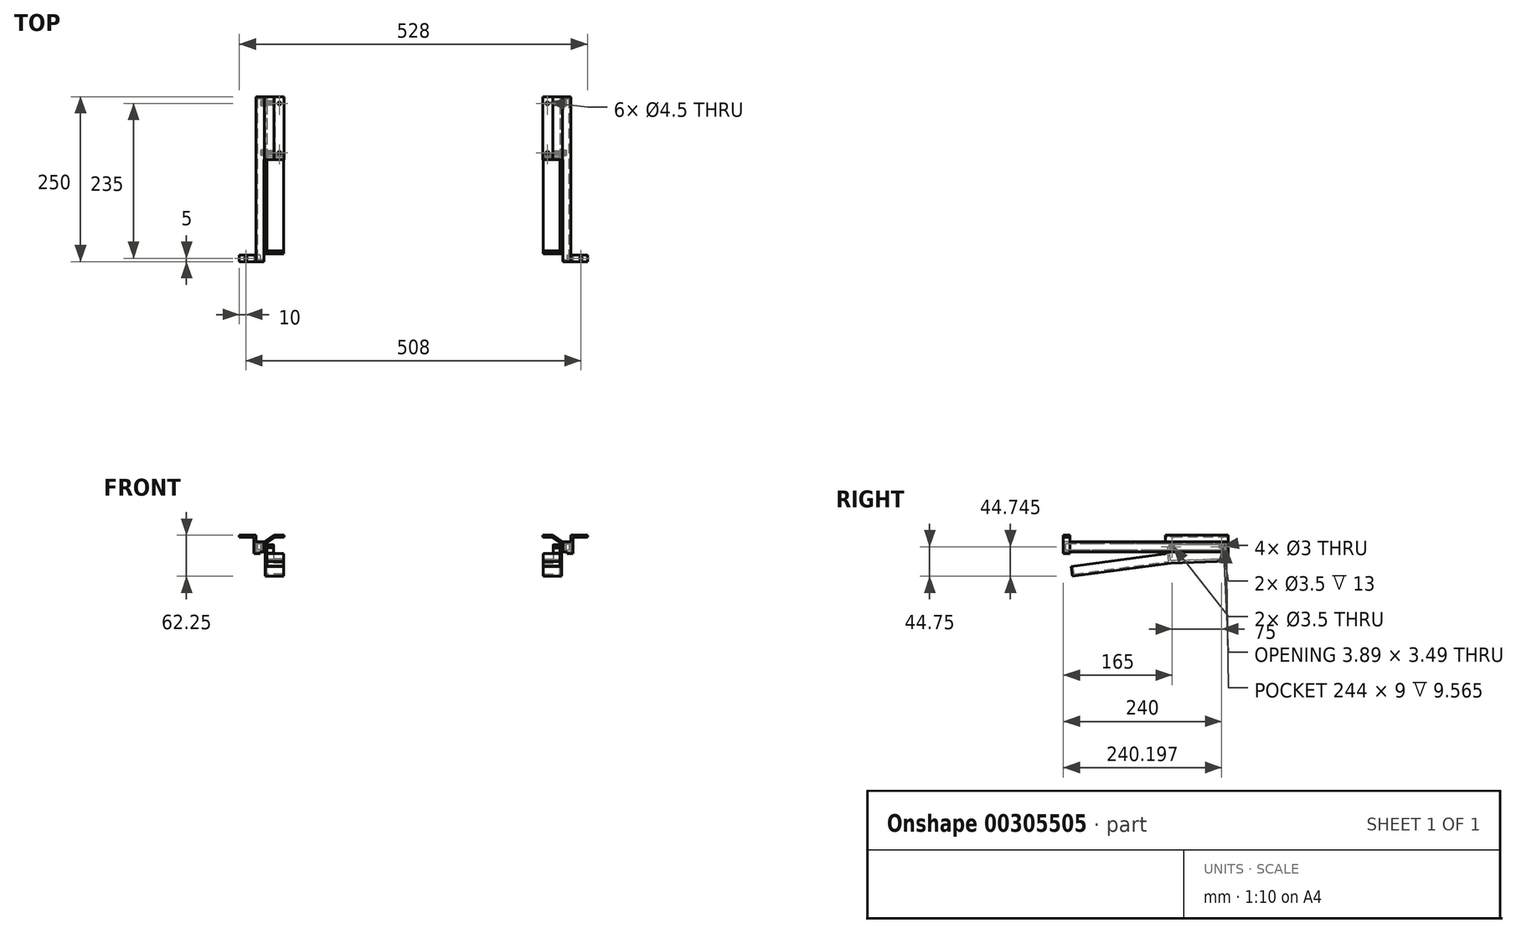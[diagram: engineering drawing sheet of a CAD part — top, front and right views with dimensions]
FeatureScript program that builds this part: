
annotation { "Feature Type Name" : "Feature", "Feature Type Description" : "" }
export const myFeature = defineFeature(function(context is Context, id is Id, definition is map)
    precondition{}
    {
        {
            var Q0;
            Q0=qCreatedBy(makeId("Right.planeOp"),FACE);
            var sketch = newSketch(context, id + "F0", { "sketchPlane" : qUnion([Q0])});
            skCircle(sketch, "E0", {"center": v(0, 0) * mm, "radius": 1.5 * mm});
            skCircle(sketch, "E1", {"center": v(0, 0) * mm, "radius": 4 * mm});
            skCircle(sketch, "E2.1.0.0", {"center": v(75, 0) * mm, "radius": 4 * mm});
            skCircle(sketch, "E2.1.0.1", {"center": v(75, 0) * mm, "radius": 1.5 * mm});
            skLineSegment(sketch, "E2.direction1", {"start": v(0, 0) * mm, "end": v(75, 0) * mm, "construction": true});
            skSolve(sketch);
        }
        {
            var Q0;
            Q0=makeQuery(id+"F0.imprint","IMPRINT",FACE,{"disambiguationData":[TD([[makeQuery(id+"F0.imprint","IMPRINT",EDGE,{"derivedFrom":sQuery(id+"F0.wireOp",EDGE,"E0")}),-1.0]])]});
            var Q1;
            Q1=makeQuery(id+"F0.imprint","IMPRINT",FACE,{"disambiguationData":[TD([[makeQuery(id+"F0.imprint","IMPRINT",EDGE,{"derivedFrom":sQuery(id+"F0.wireOp",EDGE,"E2.1.0.0")}),1.0]])]});
            extrude(context, id + "F1", {"entities" : qUnion([Q0, Q1]), "endBound" : BoundingType.SYMMETRIC, "depth" : 3 * mm});
        }
        {
            var Q0;
            Q0=qCreatedBy(makeId("Right.planeOp"),FACE);
            cPlane(context, id + "F2", {"entities" : qUnion([Q0]), "cplaneType" : CPlaneType.OFFSET, "offset" : 9 * mm, "oppositeDirection" : true, "width" : 150 * mm, "height" : 150 * mm});
        }
        {
            var Q0;
            Q0=qCreatedBy(id+"F2.planeOp",FACE);
            var sketch = newSketch(context, id + "F3", { "sketchPlane" : qUnion([Q0])});
            skLineSegment(sketch, "E3", {"start": v(0, 0) * mm, "end": v(0, 7.5) * mm, "construction": true});
            skLineSegment(sketch, "E4", {"start": v(0, 0) * mm, "end": v(85, 0) * mm, "construction": true});
            skLineSegment(sketch, "E5", {"start": v(85, 0) * mm, "end": v(85, 7.5) * mm});
            skLineSegment(sketch, "E6", {"start": v(85, 7.5) * mm, "end": v(-165, 7.5) * mm});
            skLineSegment(sketch, "E7", {"start": v(-165, 7.5) * mm, "end": v(-165, -7.5) * mm});
            skLineSegment(sketch, "E8", {"start": v(-165, -7.5) * mm, "end": v(85, -7.5) * mm});
            skLineSegment(sketch, "E9", {"start": v(85, -7.5) * mm, "end": v(85, 0) * mm});
            skSolve(sketch);
        }
        {
            var Q0;
            Q0=makeQuery(id+"F3.imprint","IMPRINT",FACE,{"disambiguationData":[TD([[makeQuery(id+"F3.imprint","IMPRINT",EDGE,{"derivedFrom":sQuery(id+"F3.wireOp",EDGE,"E5")}),1.0]])]});
            extrude(context, id + "F4", {"entities" : qUnion([Q0]), "depth" : 3 * mm});
        }
        {
            var Q0;
            Q0=makeQuery(id+"F4.opExtrude","CAP_FACE",FACE,{"disambiguationData":[OSD([sQuery(id+"F3.wireOp",EDGE,"E5"),sQuery(id+"F3.wireOp",EDGE,"E6"),sQuery(id+"F3.wireOp",EDGE,"E7"),sQuery(id+"F3.wireOp",EDGE,"E8"),sQuery(id+"F3.wireOp",EDGE,"E9")])],"isStart":false});
            var sketch = newSketch(context, id + "F5", { "sketchPlane" : qUnion([Q0])});
            skLineSegment(sketch, "E10", {"start": v(-165, 7.5) * mm, "end": v(85, 7.5) * mm});
            skLineSegment(sketch, "E11", {"start": v(85, 7.5) * mm, "end": v(85, 4.5) * mm});
            skLineSegment(sketch, "E12", {"start": v(85, 4.5) * mm, "end": v(-165, 4.5) * mm});
            skLineSegment(sketch, "E13", {"start": v(-165, 4.5) * mm, "end": v(-165, 7.5) * mm});
            skSolve(sketch);
        }
        {
            var Q0;
            Q0=makeQuery(id+"F5.imprint","IMPRINT",FACE,{"disambiguationData":[TD([[makeQuery(id+"F5.imprint","IMPRINT",EDGE,{"derivedFrom":sQuery(id+"F5.wireOp",EDGE,"E10")}),1.0]])]});
            extrude(context, id + "F6", {"entities" : qUnion([Q0]), "operationType" : NewBodyOperationType.ADD, "depth" : 10 * mm});
        }
        {
            var Q0;
            Q0=makeQuery(id+"F4.opExtrude","CAP_FACE",FACE,{"disambiguationData":[OSD([sQuery(id+"F3.wireOp",EDGE,"E5"),sQuery(id+"F3.wireOp",EDGE,"E6"),sQuery(id+"F3.wireOp",EDGE,"E7"),sQuery(id+"F3.wireOp",EDGE,"E8"),sQuery(id+"F3.wireOp",EDGE,"E9")])],"isStart":false});
            var sketch = newSketch(context, id + "F7", { "sketchPlane" : qUnion([Q0])});
            skLineSegment(sketch, "E14", {"start": v(-165, 4.5) * mm, "end": v(-165, -7.5) * mm});
            skLineSegment(sketch, "E15", {"start": v(-165, -7.5) * mm, "end": v(85, -7.5) * mm});
            skLineSegment(sketch, "E16", {"start": v(85, -7.5) * mm, "end": v(85, 4.5) * mm});
            skLineSegment(sketch, "E17.0", {"start": v(82, -4.5) * mm, "end": v(82, 4.5) * mm});
            skLineSegment(sketch, "E17.1", {"start": v(-162, -4.5) * mm, "end": v(82, -4.5) * mm});
            skLineSegment(sketch, "E17.2", {"start": v(-162, 4.5) * mm, "end": v(-162, -4.5) * mm});
            skLineSegment(sketch, "E18", {"start": v(-165, 4.5) * mm, "end": v(-162, 4.5) * mm});
            skLineSegment(sketch, "E19", {"start": v(82, 4.5) * mm, "end": v(85, 4.5) * mm});
            skSolve(sketch);
        }
        {
            var Q0;
            Q0=makeQuery(id+"F7.imprint","IMPRINT",FACE,{"disambiguationData":[TD([[makeQuery(id+"F7.imprint","IMPRINT",EDGE,{"derivedFrom":sQuery(id+"F7.wireOp",EDGE,"E14")}),1.0]])]});
            extrude(context, id + "F8", {"entities" : qUnion([Q0]), "operationType" : NewBodyOperationType.ADD, "depth" : 10 * mm});
        }
        {
            var Q0;
            Q0=qCreatedBy(makeId("Right.planeOp"),FACE);
            cPlane(context, id + "F9", {"entities" : qUnion([Q0]), "cplaneType" : CPlaneType.OFFSET, "offset" : 5 * mm, "width" : 150 * mm, "height" : 150 * mm});
        }
        {
            var Q0;
            Q0=qCreatedBy(id+"F9.planeOp",FACE);
            var sketch = newSketch(context, id + "F10", { "sketchPlane" : qUnion([Q0])});
            skLineSegment(sketch, "E20", {"start": v(0, 0) * mm, "end": v(85, 0) * mm, "construction": true});
            skLineSegment(sketch, "E21", {"start": v(85, 0) * mm, "end": v(85, 3) * mm, "construction": true});
            skLineSegment(sketch, "E22", {"start": v(85, 3) * mm, "end": v(-5, 3) * mm});
            skLineSegment(sketch, "E23", {"start": v(-5, 3) * mm, "end": v(-155, 3) * mm, "construction": true});
            skLineSegment(sketch, "E24", {"start": v(-155, 3) * mm, "end": v(-155, -17) * mm, "construction": true});
            skLineSegment(sketch, "E25", {"start": v(-155, -17) * mm, "end": v(-5, 3) * mm});
            skLineSegment(sketch, "E26", {"start": v(-155, -17) * mm, "end": v(-151.3, -44.75) * mm});
            skLineSegment(sketch, "E27", {"start": v(-151.3, -44.75) * mm, "end": v(85, -34.74) * mm});
            skLineSegment(sketch, "E28", {"start": v(85, 3) * mm, "end": v(85, -34.74) * mm});
            skSolve(sketch);
        }
        {
            var Q0;
            Q0=makeQuery(id+"F10.imprint","IMPRINT",FACE,{"disambiguationData":[TD([[makeQuery(id+"F10.imprint","IMPRINT",EDGE,{"derivedFrom":sQuery(id+"F10.wireOp",EDGE,"E22")}),1.0]])]});
            extrude(context, id + "F11", {"entities" : qUnion([Q0]), "depth" : 3 * mm});
        }
        {
            var Q0;
            Q0=makeQuery(id+"F11.opExtrude","CAP_FACE",FACE,{"disambiguationData":[OSD([sQuery(id+"F10.wireOp",EDGE,"E22"),sQuery(id+"F10.wireOp",EDGE,"E25"),sQuery(id+"F10.wireOp",EDGE,"E26"),sQuery(id+"F10.wireOp",EDGE,"E27"),sQuery(id+"F10.wireOp",EDGE,"E28")])],"isStart":false});
            var sketch = newSketch(context, id + "F12", { "sketchPlane" : qUnion([Q0])});
            skLineSegment(sketch, "E29", {"start": v(0, 0) * mm, "end": v(75, 0) * mm, "construction": true});
            skCircle(sketch, "E30", {"center": v(0, 0) * mm, "radius": 1.75 * mm});
            skCircle(sketch, "E31", {"center": v(75, 0) * mm, "radius": 1.75 * mm});
            skSolve(sketch);
        }
        {
            var Q0;
            Q0=makeQuery(id+"F12.imprint","IMPRINT",FACE,{"disambiguationData":[TD([[makeQuery(id+"F12.imprint","IMPRINT",EDGE,{"derivedFrom":sQuery(id+"F12.wireOp",EDGE,"E30")}),1.0]])]});
            var Q1;
            Q1=makeQuery(id+"F12.imprint","IMPRINT",FACE,{"disambiguationData":[TD([[makeQuery(id+"F12.imprint","IMPRINT",EDGE,{"derivedFrom":sQuery(id+"F12.wireOp",EDGE,"E31")}),1.0]])]});
            extrude(context, id + "F13", {"entities" : qUnion([Q0, Q1]), "operationType" : NewBodyOperationType.REMOVE, "endBound" : BoundingType.UP_TO_NEXT, "oppositeDirection" : true, "depth" : 25 * mm});
        }
        {
            var Q0;
            Q0=makeQuery(id+"F11.opExtrude","CAP_FACE",FACE,{"disambiguationData":[OSD([sQuery(id+"F10.wireOp",EDGE,"E22"),sQuery(id+"F10.wireOp",EDGE,"E25"),sQuery(id+"F10.wireOp",EDGE,"E26"),sQuery(id+"F10.wireOp",EDGE,"E27"),sQuery(id+"F10.wireOp",EDGE,"E28")])],"isStart":false});
            var sketch = newSketch(context, id + "F14", { "sketchPlane" : qUnion([Q0])});
            skLineSegment(sketch, "E32", {"start": v(-151.3, -44.75) * mm, "end": v(-153.28, -29.89) * mm});
            skLineSegment(sketch, "E33", {"start": v(-153.28, -29.89) * mm, "end": v(-150.3, -29.49) * mm});
            skLineSegment(sketch, "E34.0", {"start": v(-148.72, -41.38) * mm, "end": v(-150.3, -29.49) * mm});
            skLineSegment(sketch, "E35", {"start": v(-148.72, -41.38) * mm, "end": v(-5, -22.22) * mm});
            skLineSegment(sketch, "E36", {"start": v(-5, -22.22) * mm, "end": v(-6.58, -10.33) * mm});
            skLineSegment(sketch, "E37.0", {"start": v(-2.09, -21.33) * mm, "end": v(-3.57, -10.19) * mm});
            skLineSegment(sketch, "E37.1", {"start": v(-151.3, -44.75) * mm, "end": v(-1.62, -24.8) * mm});
            skLineSegment(sketch, "E38", {"start": v(-6.58, -10.33) * mm, "end": v(-3.57, -10.19) * mm});
            skLineSegment(sketch, "E39", {"start": v(-1.62, -24.8) * mm, "end": v(85, -21.77) * mm});
            skLineSegment(sketch, "E40", {"start": v(85, -21.77) * mm, "end": v(85, -18.77) * mm});
            skLineSegment(sketch, "E41", {"start": v(85, -18.77) * mm, "end": v(-2.09, -21.33) * mm});
            skPoint(sketch, "E42.trimOffspring.end.orphan", {"position": v(-32.21, -22.22) * mm});
            skSolve(sketch);
        }
        {
            var Q0;
            Q0=makeQuery(id+"F14.imprint","IMPRINT",FACE,{"disambiguationData":[TD([[makeQuery(id+"F14.imprint","IMPRINT",EDGE,{"derivedFrom":sQuery(id+"F14.wireOp",EDGE,"E32")}),1.0]])]});
            extrude(context, id + "F15", {"entities" : qUnion([Q0]), "operationType" : NewBodyOperationType.ADD, "depth" : 25 * mm});
        }
        {
            var Q0;
            Q0=qCreatedBy(id+"F9.planeOp",FACE);
            cPlane(context, id + "F16", {"entities" : qUnion([Q0]), "cplaneType" : CPlaneType.OFFSET, "offset" : 225 * mm, "width" : 150 * mm, "height" : 150 * mm});
        }
        {
            var Q0;
            Q0=makeQuery(id+"F4.opExtrude","SWEPT_BODY",BODY,{"disambiguationData":[OSD([sQuery(id+"F3.wireOp",EDGE,"E5"),sQuery(id+"F3.wireOp",EDGE,"E6"),sQuery(id+"F3.wireOp",EDGE,"E7"),sQuery(id+"F3.wireOp",EDGE,"E8"),sQuery(id+"F3.wireOp",EDGE,"E9")])]});
            var Q1;
            Q1=makeQuery(id+"F11.opExtrude","SWEPT_BODY",BODY,{"disambiguationData":[OSD([sQuery(id+"F10.wireOp",EDGE,"E22"),sQuery(id+"F10.wireOp",EDGE,"E25"),sQuery(id+"F10.wireOp",EDGE,"E26"),sQuery(id+"F10.wireOp",EDGE,"E27"),sQuery(id+"F10.wireOp",EDGE,"E28")])]});
            var Q2;
            Q2=makeQuery(id+"F1.opExtrude","SWEPT_BODY",BODY,{"disambiguationData":[OSD([sQuery(id+"F0.wireOp",EDGE,"E0"),sQuery(id+"F0.wireOp",EDGE,"E1")])]});
            var Q3;
            Q3=makeQuery(id+"F1.opExtrude","SWEPT_BODY",BODY,{"disambiguationData":[OSD([sQuery(id+"F0.wireOp",EDGE,"E2.1.0.0"),sQuery(id+"F0.wireOp",EDGE,"E2.1.0.1")])]});
            var Q4;
            Q4=qCreatedBy(id+"F16.planeOp",FACE);
            mirror(context, id + "F17", {"entities" : qUnion([Q0, Q1, Q2, Q3]), "mirrorPlane" : qUnion([Q4])});
        }
        {
            var Q0;
            Q0=makeQuery(id+"F11.opExtrude","CAP_FACE",FACE,{"disambiguationData":[OSD([sQuery(id+"F10.wireOp",EDGE,"E22"),sQuery(id+"F10.wireOp",EDGE,"E25"),sQuery(id+"F10.wireOp",EDGE,"E26"),sQuery(id+"F10.wireOp",EDGE,"E27"),sQuery(id+"F10.wireOp",EDGE,"E28")])],"isStart":false});
            var sketch = newSketch(context, id + "F18", { "sketchPlane" : qUnion([Q0])});
            skArc(sketch, "E43", {"start": v(0.94, -1.47) * mm, "mid": v(0.78, 1.57) * mm, "end": v(-1.74, -0.14) * mm});
            skArc(sketch, "E44", {"start": v(0, -3) * mm, "mid": v(0.64, 2.93) * mm, "end": v(-1.25, -2.73) * mm});
            skLineSegment(sketch, "E45", {"start": v(0, 0) * mm, "end": v(0, -31.78) * mm, "construction": true});
            skLineSegment(sketch, "E46.1.0.0", {"start": v(76.5, -2.79) * mm, "end": v(76.7, -19.01) * mm});
            skLineSegment(sketch, "E46.1.0.1", {"start": v(74.14, -2.73) * mm, "end": v(73.42, -19.1) * mm});
            skLineSegment(sketch, "E46.1.0.2", {"start": v(75.4, 0) * mm, "end": v(75.4, -31.78) * mm, "construction": true});
            skCircle(sketch, "E46.1.0.4", {"center": v(75.4, 0) * mm, "radius": 1.75 * mm});
            skLineSegment(sketch, "E46.1.0.5", {"start": v(73.42, -19.1) * mm, "end": v(76.7, -19.01) * mm});
            skLineSegment(sketch, "E46.direction1", {"start": v(-1.58, -19.1) * mm, "end": v(73.42, -19.1) * mm, "construction": true});
            skLineSegment(sketch, "E47", {"start": v(-5.08, -10.26) * mm, "end": v(0, 0) * mm, "construction": true});
            skLineSegment(sketch, "E48.0", {"start": v(-6.6, -9.95) * mm, "end": v(-1.74, -0.14) * mm});
            skLineSegment(sketch, "E49.0", {"start": v(-3.02, -9.48) * mm, "end": v(0.94, -1.47) * mm});
            skLineSegment(sketch, "E50", {"start": v(-6.58, -10.33) * mm, "end": v(-6.6, -9.95) * mm});
            skLineSegment(sketch, "E51", {"start": v(-6.58, -10.33) * mm, "end": v(-3.57, -10.19) * mm});
            skLineSegment(sketch, "E52", {"start": v(-3.57, -10.19) * mm, "end": v(-3.02, -9.48) * mm});
            skPoint(sketch, "E53.orphan", {"position": v(-6.78, -10.33) * mm});
            skPoint(sketch, "E54.orphan", {"position": v(-3.37, -10.19) * mm});
            skPoint(sketch, "E55.orphan", {"position": v(76.5, -2.6) * mm});
            skPoint(sketch, "E56.orphan", {"position": v(75.4, -3) * mm});
            skArc(sketch, "E57", {"start": v(76.5, -2.79) * mm, "mid": v(75.47, 3) * mm, "end": v(74.14, -2.73) * mm});
            skSolve(sketch);
        }
        {
            var Q0;
            {var subQ10=sQuery(id+"F18.wireOp",EDGE,"E50");Q0=makeQuery(id+"F18.imprint","IMPRINT",FACE,{"disambiguationData":[TD([[makeQuery(id+"F18.imprint","IMPRINT",EDGE,{"derivedFrom":subQ10}),-1.0]])]});}
            var Q1;
            {var subQ1=sQuery(id+"F18.wireOp",EDGE,"E43");Q1=makeQuery(id+"F18.imprint","IMPRINT",FACE,{"disambiguationData":[TD([[makeQuery(id+"F18.imprint","IMPRINT",EDGE,{"derivedFrom":subQ1}),-1.0]])]});}
            var Q2;
            {var subQ6=sQuery(id+"F18.wireOp",EDGE,"E46.1.0.0");Q2=makeQuery(id+"F18.imprint","IMPRINT",FACE,{"disambiguationData":[TD([[makeQuery(id+"F18.imprint","IMPRINT",EDGE,{"derivedFrom":subQ6}),-1.0]])]});}
            extrude(context, id + "F19", {"entities" : qUnion([Q0, Q1, Q2]), "operationType" : NewBodyOperationType.ADD, "depth" : 10 * mm});
        }
        {
            var Q0;
            Q0=makeQuery(id+"F17.opPattern","COPY",BODY,{"derivedFrom":makeQuery(id+"F11.opExtrude","SWEPT_BODY",BODY,{"disambiguationData":[OSD([sQuery(id+"F10.wireOp",EDGE,"E22"),sQuery(id+"F10.wireOp",EDGE,"E25"),sQuery(id+"F10.wireOp",EDGE,"E26"),sQuery(id+"F10.wireOp",EDGE,"E27"),sQuery(id+"F10.wireOp",EDGE,"E28")])]}),"instanceName":"1"});
            deleteBodies(context, id + "F20", {"entities" : qUnion([Q0])});
        }
        {
            var Q0;
            Q0=makeQuery(id+"F11.opExtrude","SWEPT_BODY",BODY,{"disambiguationData":[OSD([sQuery(id+"F10.wireOp",EDGE,"E22"),sQuery(id+"F10.wireOp",EDGE,"E25"),sQuery(id+"F10.wireOp",EDGE,"E26"),sQuery(id+"F10.wireOp",EDGE,"E27"),sQuery(id+"F10.wireOp",EDGE,"E28")])]});
            var Q1;
            Q1=qCreatedBy(id+"F16.planeOp",FACE);
            mirror(context, id + "F21", {"entities" : qUnion([Q0]), "mirrorPlane" : qUnion([Q1])});
        }
        {
            var Q0;
            Q0=makeQuery(id+"F21.opPattern","COPY",BODY,{"derivedFrom":makeQuery(id+"F11.opExtrude","SWEPT_BODY",BODY,{"disambiguationData":[OSD([sQuery(id+"F10.wireOp",EDGE,"E22"),sQuery(id+"F10.wireOp",EDGE,"E25"),sQuery(id+"F10.wireOp",EDGE,"E26"),sQuery(id+"F10.wireOp",EDGE,"E27"),sQuery(id+"F10.wireOp",EDGE,"E28")])]}),"instanceName":"1"});
            deleteBodies(context, id + "F22", {"entities" : qUnion([Q0])});
        }
        {
            var Q0;
            {var subQ0=sQuery(id+"F10.wireOp",EDGE,"E28");var subQ1=sQuery(id+"F10.wireOp",EDGE,"E27");var subQ2=sQuery(id+"F10.wireOp",EDGE,"E26");Q0=makeQuery(id+"F15.boolean.opBoolean","SPLIT",FACE,{"disambiguationData":[TD([makeQuery(id+"F11.opExtrude","SWEPT_FACE",FACE,{"disambiguationData":[OSD([subQ1])]})])],"derivedFrom":makeQuery(id+"F11.opExtrude","CAP_FACE",FACE,{"disambiguationData":[OSD([sQuery(id+"F10.wireOp",EDGE,"E22"),sQuery(id+"F10.wireOp",EDGE,"E25"),subQ2,subQ1,subQ0])],"isStart":false})});}
            var sketch = newSketch(context, id + "F23", { "sketchPlane" : qUnion([Q0])});
            skLineSegment(sketch, "E58", {"start": v(-151.3, -44.75) * mm, "end": v(-1.62, -24.8) * mm});
            skLineSegment(sketch, "E59", {"start": v(-1.62, -24.8) * mm, "end": v(85, -21.77) * mm});
            skLineSegment(sketch, "E60", {"start": v(85, -21.77) * mm, "end": v(85, -34.74) * mm});
            skLineSegment(sketch, "E61", {"start": v(85, -34.74) * mm, "end": v(-151.3, -44.75) * mm});
            skSolve(sketch);
        }
        {
            var Q0;
            Q0=makeQuery(id+"F23.imprint","IMPRINT",FACE,{"disambiguationData":[TD([[makeQuery(id+"F23.imprint","IMPRINT",EDGE,{"derivedFrom":sQuery(id+"F23.wireOp",EDGE,"E58")}),-1.0]])]});
            extrude(context, id + "F24", {"entities" : qUnion([Q0]), "operationType" : NewBodyOperationType.REMOVE, "endBound" : BoundingType.UP_TO_NEXT, "oppositeDirection" : true, "depth" : 25 * mm});
        }
        {
            var Q0;
            Q0=makeQuery(id+"F11.opExtrude","SWEPT_BODY",BODY,{"disambiguationData":[OSD([sQuery(id+"F10.wireOp",EDGE,"E22"),sQuery(id+"F10.wireOp",EDGE,"E25"),sQuery(id+"F10.wireOp",EDGE,"E26"),sQuery(id+"F10.wireOp",EDGE,"E27"),sQuery(id+"F10.wireOp",EDGE,"E28")])]});
            var Q1;
            Q1=qCreatedBy(id+"F16.planeOp",FACE);
            mirror(context, id + "F25", {"entities" : qUnion([Q0]), "mirrorPlane" : qUnion([Q1])});
        }
        {
            var Q0;
            Q0=makeQuery(id+"F8.boolean.opBoolean","MERGE",FACE,{"derivedFrom":[makeQuery(id+"F6.boolean.opBoolean","MERGE",FACE,{"derivedFrom":[makeQuery(id+"F4.opExtrude","SWEPT_FACE",FACE,{"disambiguationData":[OSD([sQuery(id+"F3.wireOp",EDGE,"E7")])]}),makeQuery(id+"F6.opExtrude","SWEPT_FACE",FACE,{"disambiguationData":[OSD([sQuery(id+"F5.wireOp",EDGE,"E13")])]})]}),makeQuery(id+"F8.opExtrude","SWEPT_FACE",FACE,{"disambiguationData":[OSD([sQuery(id+"F7.wireOp",EDGE,"E14")])]})]});
            var sketch = newSketch(context, id + "F26", { "sketchPlane" : qUnion([Q0])});
            skLineSegment(sketch, "E62", {"start": v(4, 7.5) * mm, "end": v(18.76, 17.5) * mm});
            skLineSegment(sketch, "E63", {"start": v(18.76, 17.5) * mm, "end": v(33.76, 17.5) * mm});
            skLineSegment(sketch, "E64", {"start": v(33.76, 17.5) * mm, "end": v(33.76, 14.5) * mm});
            skLineSegment(sketch, "E65.0", {"start": v(19.68, 14.5) * mm, "end": v(33.76, 14.5) * mm});
            skLineSegment(sketch, "E65.1", {"start": v(5.68, 5.02) * mm, "end": v(19.68, 14.5) * mm});
            skLineSegment(sketch, "E66", {"start": v(5.68, 5.02) * mm, "end": v(4.93, 4.5) * mm});
            skLineSegment(sketch, "E67", {"start": v(4, 4.5) * mm, "end": v(4, 7.5) * mm});
            skLineSegment(sketch, "E68", {"start": v(4.93, 4.5) * mm, "end": v(4, 4.5) * mm});
            skSolve(sketch);
        }
        {
            var Q0;
            Q0=makeQuery(id+"F26.imprint","IMPRINT",FACE,{"disambiguationData":[TD([[makeQuery(id+"F26.imprint","IMPRINT",EDGE,{"derivedFrom":sQuery(id+"F26.wireOp",EDGE,"E62")}),-1.0]])]});
            extrude(context, id + "F27", {"entities" : qUnion([Q0]), "operationType" : NewBodyOperationType.ADD, "oppositeDirection" : true, "depth" : 250 * mm});
        }
        {
            var Q0;
            Q0=makeQuery(id+"F27.opExtrude","SWEPT_FACE",FACE,{"disambiguationData":[OSD([sQuery(id+"F26.wireOp",EDGE,"E63")])]});
            var sketch = newSketch(context, id + "F28", { "sketchPlane" : qUnion([Q0])});
            skLineSegment(sketch, "E69", {"start": v(33.76, 85) * mm, "end": v(26.76, 85) * mm, "construction": true});
            skLineSegment(sketch, "E70", {"start": v(26.76, 85) * mm, "end": v(26.76, 75) * mm, "construction": true});
            skLineSegment(sketch, "E71", {"start": v(26.76, 75) * mm, "end": v(26.76, 0) * mm, "construction": true});
            skCircle(sketch, "E72", {"center": v(26.76, 75) * mm, "radius": 2.25 * mm});
            skCircle(sketch, "E73", {"center": v(26.76, 0) * mm, "radius": 2.25 * mm});
            skSolve(sketch);
        }
        {
            var Q0;
            Q0=makeQuery(id+"F28.imprint","IMPRINT",FACE,{"disambiguationData":[TD([[makeQuery(id+"F28.imprint","IMPRINT",EDGE,{"derivedFrom":sQuery(id+"F28.wireOp",EDGE,"E72")}),1.0]])]});
            var Q1;
            Q1=makeQuery(id+"F28.imprint","IMPRINT",FACE,{"disambiguationData":[TD([[makeQuery(id+"F28.imprint","IMPRINT",EDGE,{"derivedFrom":sQuery(id+"F28.wireOp",EDGE,"E73")}),1.0]])]});
            extrude(context, id + "F29", {"entities" : qUnion([Q0, Q1]), "operationType" : NewBodyOperationType.REMOVE, "endBound" : BoundingType.UP_TO_NEXT, "oppositeDirection" : true, "depth" : 25 * mm});
        }
        {
            var Q0;
            Q0=makeQuery(id+"F27.opExtrude","SWEPT_FACE",FACE,{"disambiguationData":[OSD([sQuery(id+"F26.wireOp",EDGE,"E63")])]});
            var sketch = newSketch(context, id + "F30", { "sketchPlane" : qUnion([Q0])});
            skLineSegment(sketch, "E74", {"start": v(26.76, 0) * mm, "end": v(26.76, -10) * mm, "construction": true});
            skLineSegment(sketch, "E75", {"start": v(26.76, -10) * mm, "end": v(3.57, -10) * mm});
            skLineSegment(sketch, "E76", {"start": v(3.57, -10) * mm, "end": v(3.57, -165) * mm});
            skLineSegment(sketch, "E77", {"start": v(26.76, -10) * mm, "end": v(33.76, -10) * mm});
            skLineSegment(sketch, "E78", {"start": v(33.76, -10) * mm, "end": v(33.76, -165) * mm});
            skLineSegment(sketch, "E79", {"start": v(33.76, -165) * mm, "end": v(3.57, -165) * mm});
            skSolve(sketch);
        }
        {
            var Q0;
            {var subQ4=sQuery(id+"F30.wireOp",EDGE,"E77");Q0=makeQuery(id+"F30.imprint","IMPRINT",FACE,{"disambiguationData":[TD([[makeQuery(id+"F30.imprint","IMPRINT",EDGE,{"derivedFrom":subQ4}),-1.0]])]});}
            var Q1;
            {var subQ0=sQuery(id+"F30.wireOp",EDGE,"E76");Q1=makeQuery(id+"F30.imprint","IMPRINT",FACE,{"disambiguationData":[TD([[makeQuery(id+"F30.imprint","IMPRINT",EDGE,{"derivedFrom":subQ0}),1.0]])]});}
            extrude(context, id + "F31", {"entities" : qUnion([Q0, Q1]), "operationType" : NewBodyOperationType.REMOVE, "endBound" : BoundingType.UP_TO_NEXT, "oppositeDirection" : true, "depth" : 25 * mm});
        }
        {
            var Q0;
            Q0=makeQuery(id+"F17.opPattern","COPY",BODY,{"derivedFrom":makeQuery(id+"F4.opExtrude","SWEPT_BODY",BODY,{"disambiguationData":[OSD([sQuery(id+"F3.wireOp",EDGE,"E5"),sQuery(id+"F3.wireOp",EDGE,"E6"),sQuery(id+"F3.wireOp",EDGE,"E7"),sQuery(id+"F3.wireOp",EDGE,"E8"),sQuery(id+"F3.wireOp",EDGE,"E9")])]}),"instanceName":"1"});
            deleteBodies(context, id + "F32", {"entities" : qUnion([Q0])});
        }
        {
            var Q0;
            Q0=makeQuery(id+"F4.opExtrude","SWEPT_BODY",BODY,{"disambiguationData":[OSD([sQuery(id+"F3.wireOp",EDGE,"E5"),sQuery(id+"F3.wireOp",EDGE,"E6"),sQuery(id+"F3.wireOp",EDGE,"E7"),sQuery(id+"F3.wireOp",EDGE,"E8"),sQuery(id+"F3.wireOp",EDGE,"E9")])]});
            var Q1;
            Q1=qCreatedBy(id+"F16.planeOp",FACE);
            mirror(context, id + "F33", {"entities" : qUnion([Q0]), "mirrorPlane" : qUnion([Q1])});
        }
        {
            var Q0;
            Q0=makeQuery(id+"F25.opPattern","COPY",BODY,{"derivedFrom":makeQuery(id+"F11.opExtrude","SWEPT_BODY",BODY,{"disambiguationData":[OSD([sQuery(id+"F10.wireOp",EDGE,"E22"),sQuery(id+"F10.wireOp",EDGE,"E25"),sQuery(id+"F10.wireOp",EDGE,"E26"),sQuery(id+"F10.wireOp",EDGE,"E27"),sQuery(id+"F10.wireOp",EDGE,"E28")])]}),"instanceName":"1"});
            deleteBodies(context, id + "F34", {"entities" : qUnion([Q0])});
        }
        {
            var Q0;
            {var subQ1=sQuery(id+"F10.wireOp",EDGE,"E22");var subQ2=makeQuery(id+"F11.opExtrude","SWEPT_FACE",FACE,{"disambiguationData":[OSD([subQ1])]});var subQ7=sQuery(id+"F10.wireOp",EDGE,"E28");var subQ8=sQuery(id+"F10.wireOp",EDGE,"E26");var subQ9=sQuery(id+"F10.wireOp",EDGE,"E25");var subQ10=makeQuery(id+"F11.opExtrude","CAP_FACE",FACE,{"disambiguationData":[OSD([subQ1,subQ9,subQ8,sQuery(id+"F10.wireOp",EDGE,"E27"),subQ7])],"isStart":false});var subQ11=makeQuery(id+"F11.opExtrude","SWEPT_FACE",FACE,{"disambiguationData":[OSD([subQ9])]});Q0=makeQuery(id+"F19.boolean.opBoolean","SPLIT",FACE,{"disambiguationData":[TD([subQ11])],"derivedFrom":makeQuery(id+"F15.boolean.opBoolean","SPLIT",FACE,{"disambiguationData":[TD([subQ2])],"derivedFrom":subQ10})});}
            var sketch = newSketch(context, id + "F35", { "sketchPlane" : qUnion([Q0])});
            skLineSegment(sketch, "E80", {"start": v(-153.28, -29.89) * mm, "end": v(-8.93, -10.64) * mm});
            skLineSegment(sketch, "E81", {"start": v(-8.93, -10.64) * mm, "end": v(-5, 3) * mm});
            skLineSegment(sketch, "E82", {"start": v(-5, 3) * mm, "end": v(-155, -17) * mm});
            skLineSegment(sketch, "E83", {"start": v(-155, -17) * mm, "end": v(-153.28, -29.89) * mm});
            skSolve(sketch);
        }
        {
            var Q0;
            {var subQ0=sQuery(id+"F35.wireOp",EDGE,"E81");Q0=makeQuery(id+"F35.imprint","IMPRINT",FACE,{"disambiguationData":[TD([[makeQuery(id+"F35.imprint","IMPRINT",EDGE,{"derivedFrom":subQ0}),1.0]])]});}
            extrude(context, id + "F36", {"entities" : qUnion([Q0]), "operationType" : NewBodyOperationType.REMOVE, "endBound" : BoundingType.UP_TO_NEXT, "oppositeDirection" : true, "depth" : 25 * mm});
        }
        {
            var Q0;
            Q0=makeQuery(id+"F36.boolean.opBoolean","COPY",EDGE,{"derivedFrom":makeQuery(id+"F36.opExtrude","SWEPT_EDGE",EDGE,{"disambiguationData":[OSD([sQuery(id+"F35.wireOp",EDGE,"E80"),sQuery(id+"F35.wireOp",EDGE,"E81")])]})});
            var Q1;
            {var subQ0=sQuery(id+"F10.wireOp",EDGE,"E25");var subQ1=sQuery(id+"F10.wireOp",EDGE,"E22");Q1=makeQuery(id+"F36.boolean.opBoolean","MERGE",EDGE,{"derivedFrom":[makeQuery(id+"F11.opExtrude","SWEPT_EDGE",EDGE,{"disambiguationData":[OSD([subQ1,subQ0])]}),makeQuery(id+"F36.opExtrude","SWEPT_EDGE",EDGE,{"disambiguationData":[OSD([subQ1,subQ0])]})]});}
            fillet(context, id + "F37", {"entities" : qUnion([Q0, Q1]), "radius" : 5 * mm, "tangentPropagation" : true, "allowEdgeOverflow" : false});
        }
        {
            var Q0;
            Q0=makeQuery(id+"F11.opExtrude","SWEPT_BODY",BODY,{"disambiguationData":[OSD([sQuery(id+"F10.wireOp",EDGE,"E22"),sQuery(id+"F10.wireOp",EDGE,"E25"),sQuery(id+"F10.wireOp",EDGE,"E26"),sQuery(id+"F10.wireOp",EDGE,"E27"),sQuery(id+"F10.wireOp",EDGE,"E28")])]});
            var Q1;
            Q1=qCreatedBy(id+"F16.planeOp",FACE);
            mirror(context, id + "F38", {"entities" : qUnion([Q0]), "mirrorPlane" : qUnion([Q1])});
        }
        {
            var Q0;
            Q0=makeQuery(id+"F27.boolean.opBoolean","MERGE",FACE,{"derivedFrom":[makeQuery(id+"F8.boolean.opBoolean","MERGE",FACE,{"derivedFrom":[makeQuery(id+"F6.boolean.opBoolean","MERGE",FACE,{"derivedFrom":[makeQuery(id+"F4.opExtrude","SWEPT_FACE",FACE,{"disambiguationData":[OSD([sQuery(id+"F3.wireOp",EDGE,"E7")])]}),makeQuery(id+"F6.opExtrude","SWEPT_FACE",FACE,{"disambiguationData":[OSD([sQuery(id+"F5.wireOp",EDGE,"E13")])]})]}),makeQuery(id+"F8.opExtrude","SWEPT_FACE",FACE,{"disambiguationData":[OSD([sQuery(id+"F7.wireOp",EDGE,"E14")])]})]}),makeQuery(id+"F27.opExtrude","CAP_FACE",FACE,{"disambiguationData":[OSD([sQuery(id+"F26.wireOp",EDGE,"E62"),sQuery(id+"F26.wireOp",EDGE,"E63"),sQuery(id+"F26.wireOp",EDGE,"E64"),sQuery(id+"F26.wireOp",EDGE,"E65.0"),sQuery(id+"F26.wireOp",EDGE,"E65.1"),sQuery(id+"F26.wireOp",EDGE,"E66"),sQuery(id+"F26.wireOp",EDGE,"E67"),sQuery(id+"F26.wireOp",EDGE,"E68")])],"isStart":true})]});
            var sketch = newSketch(context, id + "F39", { "sketchPlane" : qUnion([Q0])});
            skLineSegment(sketch, "E84", {"start": v(-2.72, -7.5) * mm, "end": v(-9, -7.5) * mm});
            skLineSegment(sketch, "E85", {"start": v(-9, -7.5) * mm, "end": v(-9, 17.5) * mm});
            skLineSegment(sketch, "E86", {"start": v(-9, 17.5) * mm, "end": v(-34, 17.5) * mm});
            skLineSegment(sketch, "E87", {"start": v(-2.72, -7.5) * mm, "end": v(-2.72, -10.5) * mm});
            skLineSegment(sketch, "E88", {"start": v(-34, 17.5) * mm, "end": v(-34, 14.5) * mm});
            skLineSegment(sketch, "E89.0", {"start": v(-12, 14.5) * mm, "end": v(-34, 14.5) * mm});
            skLineSegment(sketch, "E89.1", {"start": v(-12, -10.5) * mm, "end": v(-12, 14.5) * mm});
            skLineSegment(sketch, "E89.2", {"start": v(-2.72, -10.5) * mm, "end": v(-12, -10.5) * mm});
            skSolve(sketch);
        }
        {
            var Q0;
            {var subQ3=sQuery(id+"F39.wireOp",EDGE,"E84");Q0=makeQuery(id+"F39.imprint","IMPRINT",FACE,{"disambiguationData":[TD([[makeQuery(id+"F39.imprint","IMPRINT",EDGE,{"derivedFrom":subQ3}),1.0]])]});}
            extrude(context, id + "F40", {"entities" : qUnion([Q0]), "oppositeDirection" : true, "depth" : 10 * mm});
        }
        {
            var Q0;
            Q0=makeQuery(id+"F40.opExtrude","SWEPT_FACE",FACE,{"disambiguationData":[OSD([sQuery(id+"F39.wireOp",EDGE,"E86")])]});
            var sketch = newSketch(context, id + "F41", { "sketchPlane" : qUnion([Q0])});
            skLineSegment(sketch, "E90", {"start": v(-34, -160) * mm, "end": v(-24, -160) * mm, "construction": true});
            skCircle(sketch, "E91", {"center": v(-24, -160) * mm, "radius": 2.25 * mm});
            skSolve(sketch);
        }
        {
            var Q0;
            Q0=makeQuery(id+"F41.imprint","IMPRINT",FACE,{"disambiguationData":[TD([[makeQuery(id+"F41.imprint","IMPRINT",EDGE,{"derivedFrom":sQuery(id+"F41.wireOp",EDGE,"E91")}),1.0]])]});
            extrude(context, id + "F42", {"entities" : qUnion([Q0]), "operationType" : NewBodyOperationType.REMOVE, "endBound" : BoundingType.UP_TO_NEXT, "oppositeDirection" : true, "depth" : 25 * mm});
        }
        {
            var Q0;
            Q0=makeQuery(id+"F40.opExtrude","SWEPT_BODY",BODY,{"disambiguationData":[OSD([sQuery(id+"F39.wireOp",EDGE,"E84"),sQuery(id+"F39.wireOp",EDGE,"E85"),sQuery(id+"F39.wireOp",EDGE,"E86"),sQuery(id+"F39.wireOp",EDGE,"E87"),sQuery(id+"F39.wireOp",EDGE,"E88"),sQuery(id+"F39.wireOp",EDGE,"E89.0"),sQuery(id+"F39.wireOp",EDGE,"E89.1"),sQuery(id+"F39.wireOp",EDGE,"E89.2")])]});
            var Q1;
            Q1=qCreatedBy(id+"F16.planeOp",FACE);
            mirror(context, id + "F43", {"operationType" : NewBodyOperationType.ADD, "entities" : qUnion([Q0]), "mirrorPlane" : qUnion([Q1])});
        }
    });
